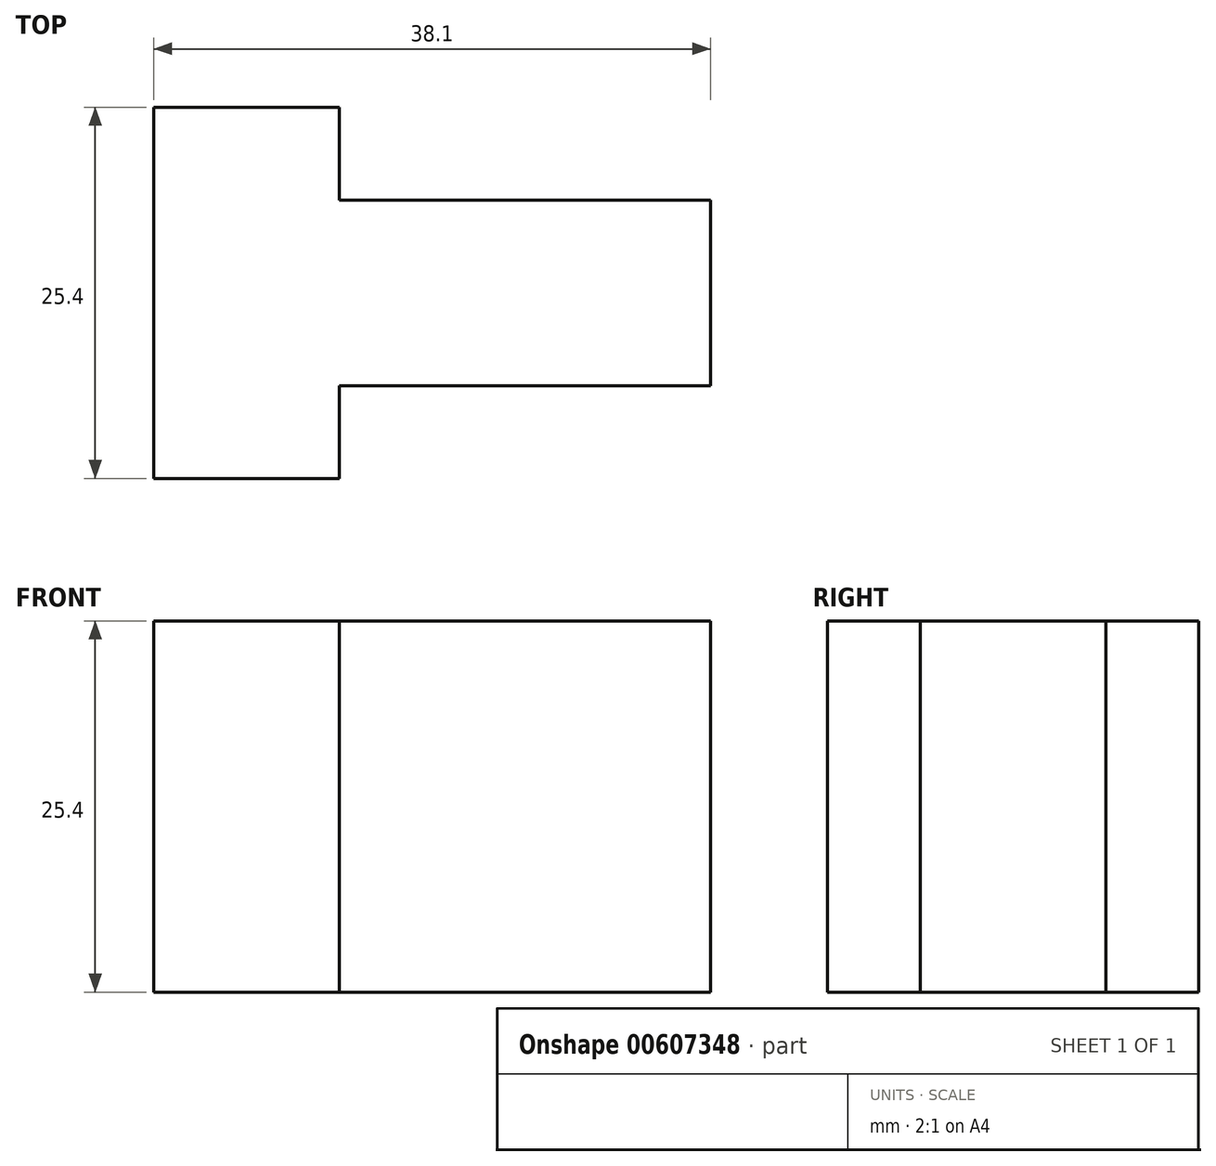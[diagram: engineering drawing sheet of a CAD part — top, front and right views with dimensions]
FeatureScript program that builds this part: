
annotation { "Feature Type Name" : "Feature", "Feature Type Description" : "" }
export const myFeature = defineFeature(function(context is Context, id is Id, definition is map)
    precondition{}
    {
        {
            var Q0;
            Q0=qCreatedBy(makeId("Top.planeOp"),FACE);
            var sketch = newSketch(context, id + "F0", { "sketchPlane" : qUnion([Q0])});
            skLineSegment(sketch, "E0", {"start": v(0, 0) * mm, "end": v(0, 25.4) * mm});
            skLineSegment(sketch, "E1", {"start": v(0, 0) * mm, "end": v(12.7, 0) * mm});
            skLineSegment(sketch, "E2", {"start": v(12.7, 0) * mm, "end": v(12.7, 6.35) * mm});
            skLineSegment(sketch, "E3", {"start": v(0, 25.4) * mm, "end": v(12.7, 25.4) * mm});
            skLineSegment(sketch, "E4", {"start": v(12.7, 25.4) * mm, "end": v(12.7, 19.05) * mm});
            skLineSegment(sketch, "E5", {"start": v(12.7, 6.35) * mm, "end": v(38.1, 6.35) * mm});
            skLineSegment(sketch, "E6", {"start": v(12.7, 19.05) * mm, "end": v(38.1, 19.05) * mm});
            skLineSegment(sketch, "E7", {"start": v(38.1, 19.05) * mm, "end": v(38.1, 6.35) * mm});
            skSolve(sketch);
        }
        {
            var Q0;
            Q0 = qSketchRegion(id + "F0", true);
            extrude(context, id + "F1", {"entities" : qUnion([Q0]), "depth" : 25.4 * mm, "offsetDistance" : 25.4 * mm});
        }
    });
